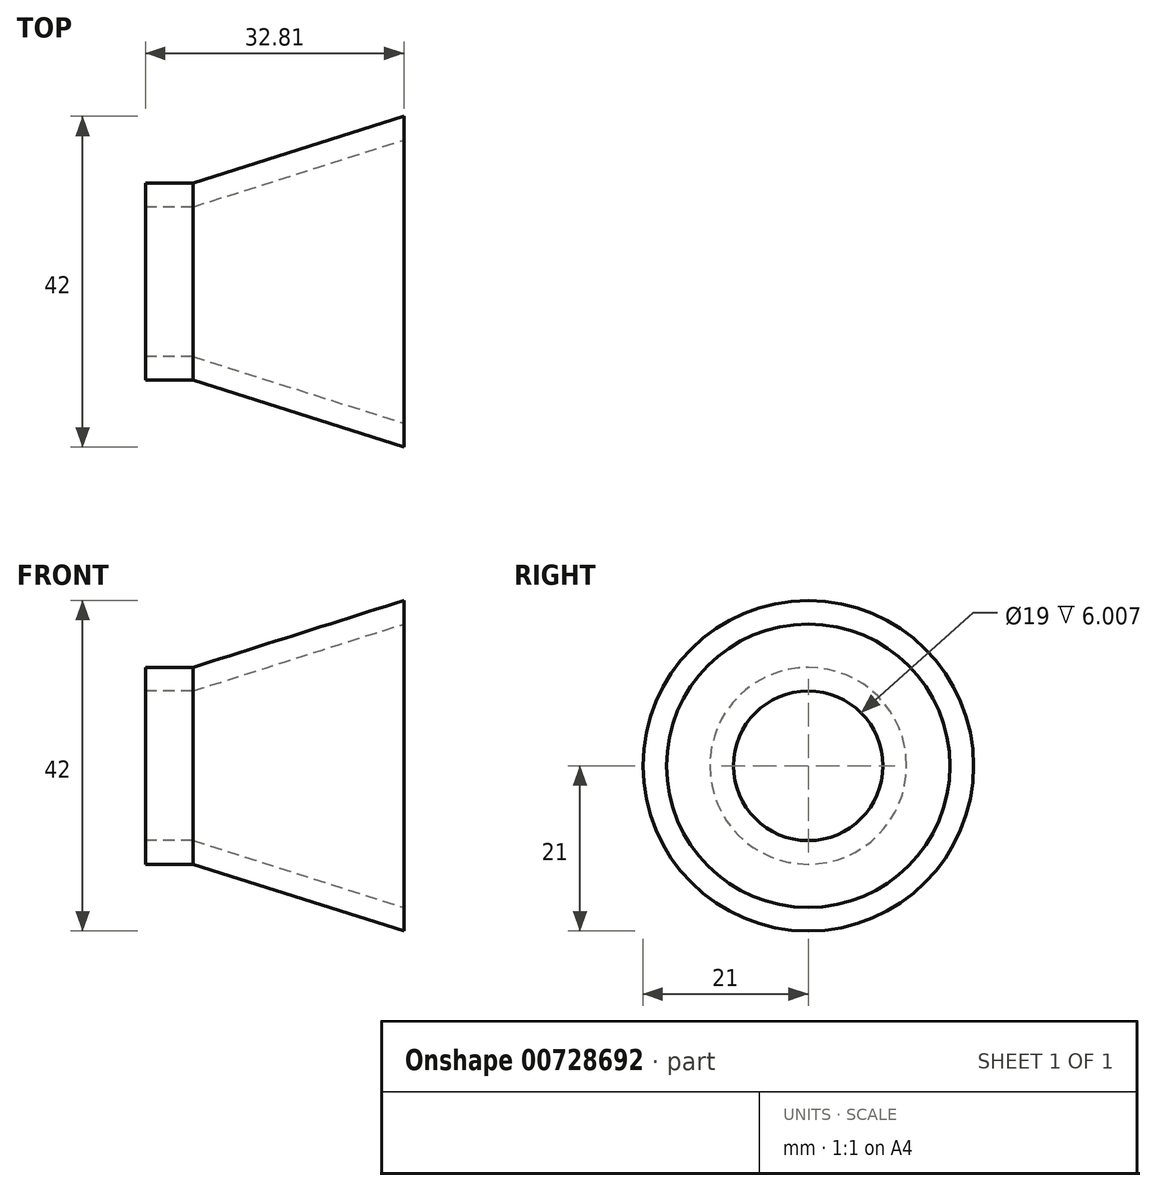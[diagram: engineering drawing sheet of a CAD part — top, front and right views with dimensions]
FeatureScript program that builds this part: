
annotation { "Feature Type Name" : "Feature", "Feature Type Description" : "" }
export const myFeature = defineFeature(function(context is Context, id is Id, definition is map)
    precondition{}
    {
        {
            var Q0;
            Q0=qCreatedBy(makeId("Front.planeOp"),FACE);
            var sketch = newSketch(context, id + "F0", { "sketchPlane" : qUnion([Q0])});
            skLineSegment(sketch, "E0", {"start": v(-13.19, 12.5) * mm, "end": v(-7.18, 12.5) * mm});
            skLineSegment(sketch, "E1", {"start": v(-7.18, 12.5) * mm, "end": v(-7.18, 12.5) * mm});
            skLineSegment(sketch, "E2", {"start": v(-7.18, 12.5) * mm, "end": v(19.62, 21) * mm});
            skLineSegment(sketch, "E3", {"start": v(19.62, 21) * mm, "end": v(19.62, 18) * mm});
            skLineSegment(sketch, "E4", {"start": v(19.62, 18) * mm, "end": v(-7.18, 9.5) * mm});
            skLineSegment(sketch, "E5", {"start": v(-7.18, 9.5) * mm, "end": v(-13.19, 9.5) * mm});
            skLineSegment(sketch, "E6", {"start": v(-13.19, 12.5) * mm, "end": v(-13.19, 9.5) * mm});
            skLineSegment(sketch, "E7", {"start": v(-21.42, 0) * mm, "end": v(29.56, 0) * mm, "construction": true});
            skSolve(sketch);
        }
        {
            var Q0;
            Q0=makeQuery(id+"F0.imprint","IMPRINT",FACE,{"disambiguationData":[TD([[makeQuery(id+"F0.imprint","IMPRINT",EDGE,{"derivedFrom":sQuery(id+"F0.wireOp",EDGE,"E0")}),-1.0]])]});
            var Q1;
            Q1=sQuery(id+"F0.wireOp",EDGE,"E7");
            revolve(context, id + "F1", {"surfaceOperationType" : NewSurfaceOperationType.NEW, "entities" : qUnion([Q0]), "axis" : qUnion([Q1]), "revolveType" : RevolveType.FULL});
        }
    });
